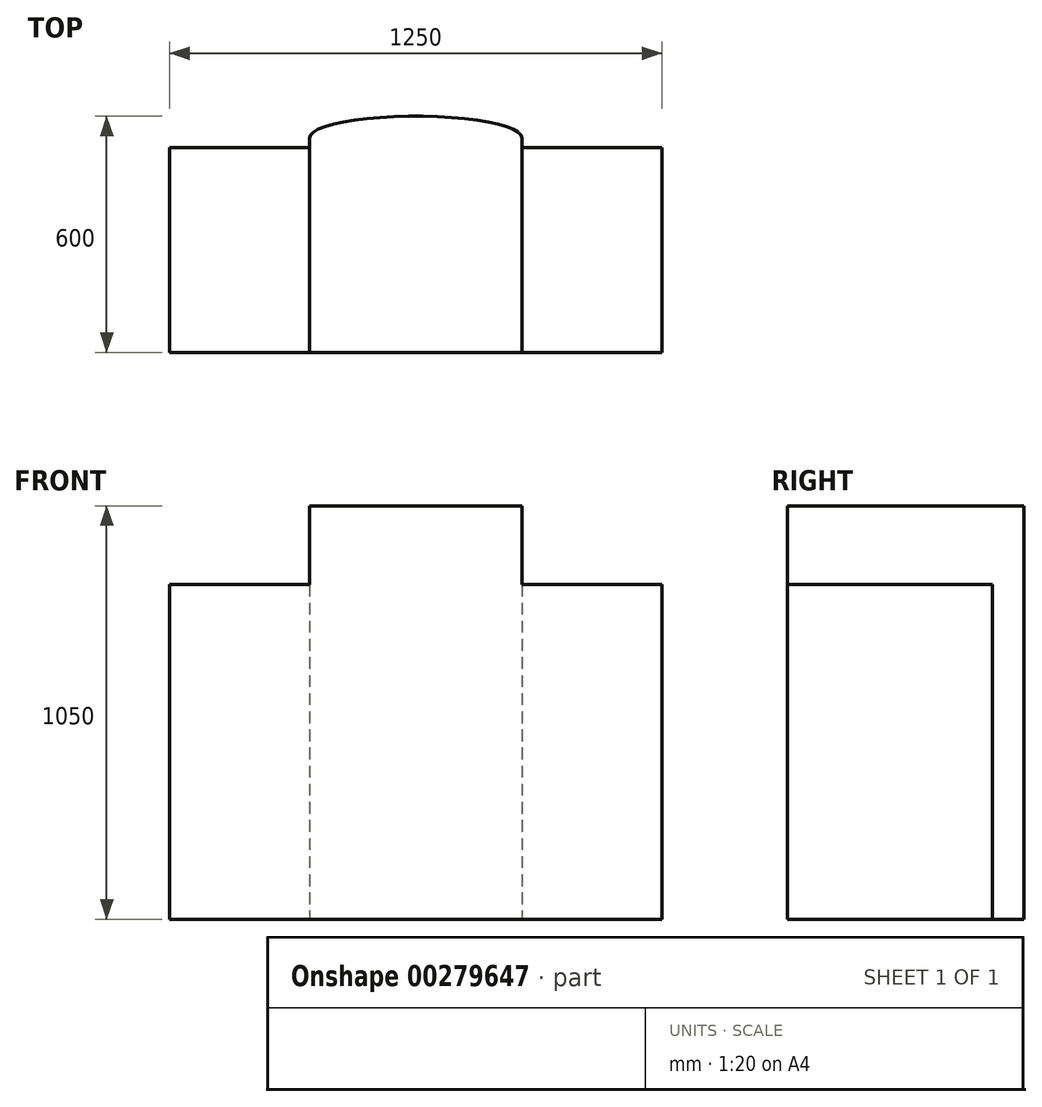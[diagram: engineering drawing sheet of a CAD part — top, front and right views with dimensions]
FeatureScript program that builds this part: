
annotation { "Feature Type Name" : "Feature", "Feature Type Description" : "" }
export const myFeature = defineFeature(function(context is Context, id is Id, definition is map)
    precondition{}
    {
        {
            var Q0;
            Q0=qCreatedBy(makeId("Top.planeOp"),FACE);
            var sketch = newSketch(context, id + "F0", { "sketchPlane" : qUnion([Q0])});
            skLineSegment(sketch, "E0", {"start": v(0, 0) * mm, "end": v(1250, 0) * mm});
            skLineSegment(sketch, "E1", {"start": v(1250, 0) * mm, "end": v(1250, 520) * mm});
            skLineSegment(sketch, "E2", {"start": v(1250, 520) * mm, "end": v(895, 520) * mm});
            skLineSegment(sketch, "E3", {"start": v(895, 520) * mm, "end": v(895, 545) * mm});
            skLineSegment(sketch, "E4", {"start": v(355, 545) * mm, "end": v(355, 520) * mm});
            skLineSegment(sketch, "E5", {"start": v(355, 520) * mm, "end": v(0, 520) * mm});
            skLineSegment(sketch, "E6", {"start": v(0, 520) * mm, "end": v(0, 0) * mm});
            skEllipticalArc(sketch, "E7", {});
            const initialGuessF0  = {"E7": [0.625, 0.545, -1, 0, 0.27, 0.055, 3.1415926535897927, 6.283185307179585]};
            skSetInitialGuess(sketch, initialGuessF0);
            skSolve(sketch);
        }
        {
            var Q0;
            Q0=makeQuery(id+"F0.imprint","IMPRINT",FACE,{"disambiguationData":[TD([[makeQuery(id+"F0.imprint","IMPRINT",EDGE,{"derivedFrom":sQuery(id+"F0.wireOp",EDGE,"E0")}),1.0]])]});
            extrude(context, id + "F1", {"entities" : qUnion([Q0]), "depth" : 850 * mm});
        }
        {
            var Q0;
            Q0=makeQuery(id+"F1.opExtrude","CAP_FACE",FACE,{"disambiguationData":[OSD([sQuery(id+"F0.wireOp",EDGE,"E0"),sQuery(id+"F0.wireOp",EDGE,"E1"),sQuery(id+"F0.wireOp",EDGE,"E2"),sQuery(id+"F0.wireOp",EDGE,"E3"),sQuery(id+"F0.wireOp",EDGE,"E4"),sQuery(id+"F0.wireOp",EDGE,"E5"),sQuery(id+"F0.wireOp",EDGE,"E6"),sQuery(id+"F0.wireOp",EDGE,"E7")])],"isStart":false});
            var sketch = newSketch(context, id + "F2", { "sketchPlane" : qUnion([Q0])});
            skEllipticalArc(sketch, "E8.0", {});
            skLineSegment(sketch, "E9.0", {"start": v(355, 0) * mm, "end": v(895, 0) * mm});
            skLineSegment(sketch, "E10.0", {"start": v(355, 545) * mm, "end": v(355, 0) * mm});
            skLineSegment(sketch, "E11.0", {"start": v(895, 0) * mm, "end": v(895, 545) * mm});
            skPoint(sketch, "E12.orphan", {"position": v(895, 520) * mm});
            skPoint(sketch, "E13.orphan", {"position": v(355, 520) * mm});
            skPoint(sketch, "E14.orphan", {"position": v(1250, 0) * mm});
            skPoint(sketch, "E15.orphan", {"position": v(0, 0) * mm});
            const initialGuessF2  = {"E8.0": [0.625, 0.545, -1, 0, 0.27, 0.055, 3.1415926535897927, 6.283185307179585]};
            skSetInitialGuess(sketch, initialGuessF2);
            skSolve(sketch);
        }
        {
            var Q0;
            {var subQ4=sQuery(id+"F2.wireOp",EDGE,"E8.0");Q0=makeQuery(id+"F2.imprint","IMPRINT",FACE,{"disambiguationData":[TD([[makeQuery(id+"F2.imprint","IMPRINT",EDGE,{"derivedFrom":subQ4}),1.0]])]});}
            extrude(context, id + "F3", {"entities" : qUnion([Q0]), "operationType" : NewBodyOperationType.ADD, "depth" : 200 * mm});
        }
    });
